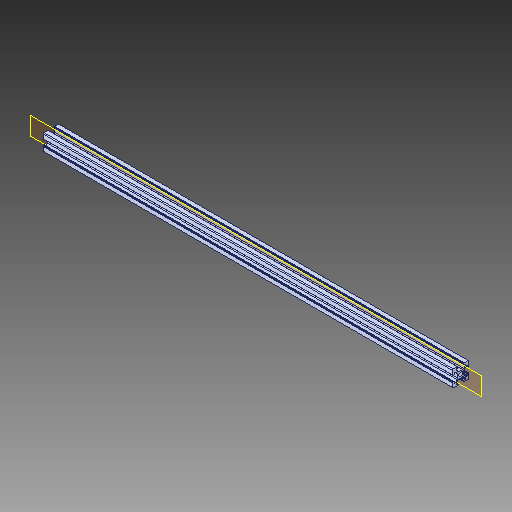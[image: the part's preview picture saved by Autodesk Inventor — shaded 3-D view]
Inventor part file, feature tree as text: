
AUTODESK INVENTOR PART (.ipt)
format: ipt  version: 2018 (Build 220112000, 112)  size: 372,224 bytes
history: native  units: in
note: dims shown in document units (in); Inventor stores cm internally (conversion verified against a paired STEP export)
features: extrude x1, sketch x1, projected_geometry x1, fillet x1
ambient origin geometry x8: Origin, YZ Plane, XZ Plane, XY Plane, X Axis, Y Axis, Z Axis, Center Point
bodies: Solid1 (feature_tree)
feature tree (4):
  extrude  "Extrusion2"  [1 undecoded]
  sketch  "Sketch3"  dims[d2=15.748in d3=0.0in]
  projected_geometry  "Projected Loop2"
  fillet  "Fillet5"  [1 undecoded]
note: 2 required parameter values undecoded (feature->parameter linkage not recoverable at this tier; creation-order binding heuristic only, values carry confidence <= 0.55)
